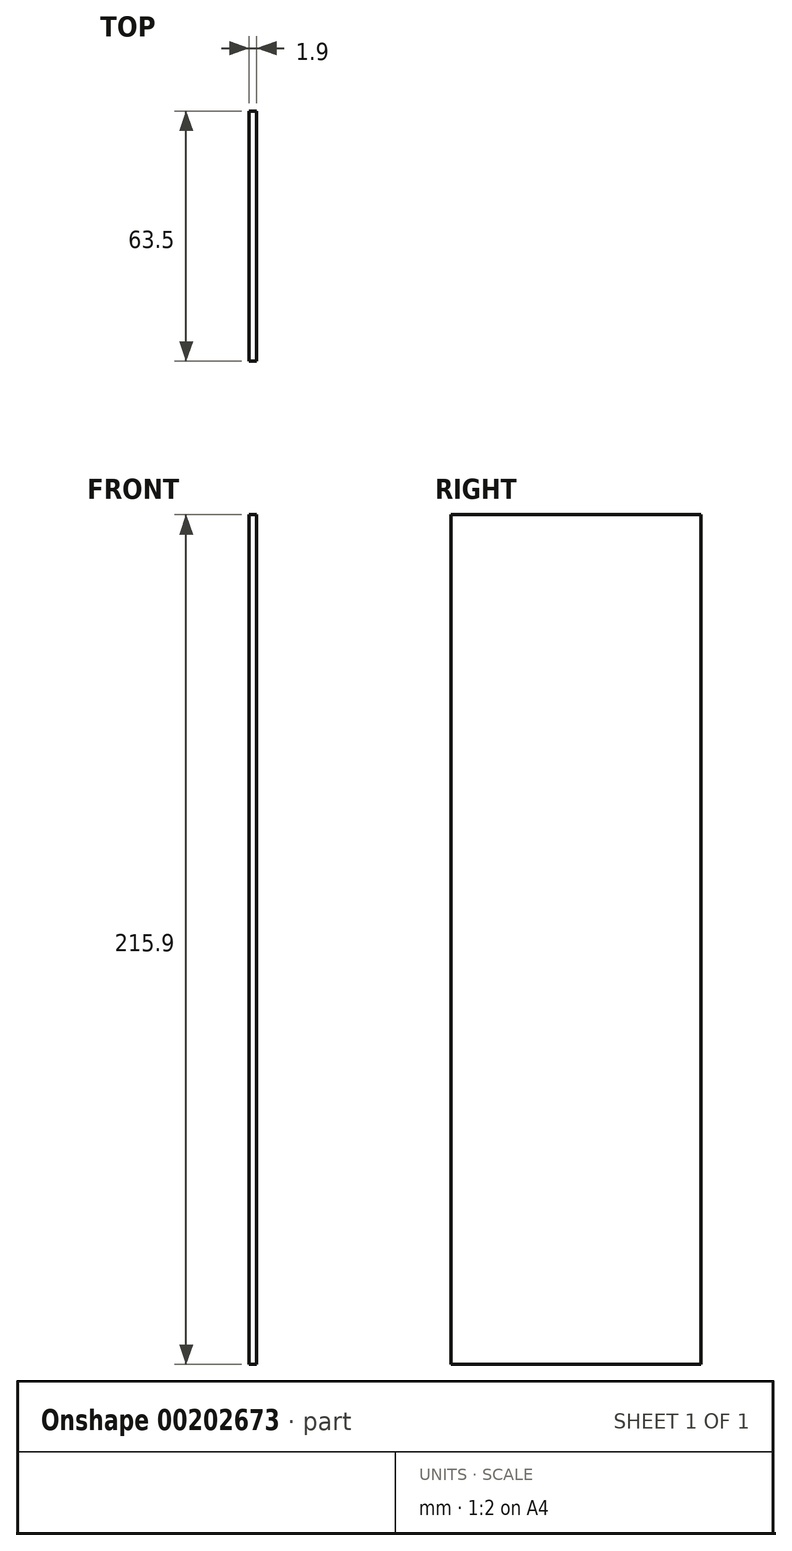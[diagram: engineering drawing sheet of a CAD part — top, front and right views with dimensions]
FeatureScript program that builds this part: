
annotation { "Feature Type Name" : "Feature", "Feature Type Description" : "" }
export const myFeature = defineFeature(function(context is Context, id is Id, definition is map)
    precondition{}
    {
        {
            var Q0;
            Q0=qCreatedBy(makeId("Right.planeOp"),FACE);
            var sketch = newSketch(context, id + "F0", { "sketchPlane" : qUnion([Q0])});
            skLineSegment(sketch, "E0.bottom", {"start": v(31.75, 107.95) * mm, "end": v(-31.75, 107.95) * mm});
            skLineSegment(sketch, "E0.top", {"start": v(31.75, -107.95) * mm, "end": v(-31.75, -107.95) * mm});
            skLineSegment(sketch, "E0.left", {"start": v(31.75, 107.95) * mm, "end": v(31.75, -107.95) * mm});
            skLineSegment(sketch, "E0.right", {"start": v(-31.75, 107.95) * mm, "end": v(-31.75, -107.95) * mm});
            skPoint(sketch, "E0.middle", {"position": v(0, 0) * mm});
            skSolve(sketch);
        }
        {
            var Q0;
            Q0 = qSketchRegion(id + "F0", true);
            extrude(context, id + "F1", {"entities" : qUnion([Q0]), "depth" : 1.9 * mm});
        }
    });
